# Revit family: Festpunkt Typ AK, T-Stahl, Ø 15 bis  60
name_source: partatom
category: HLS-Bauteile
revit_build: Autodesk Revit 2017 (Build: 20190507_1515(x64)
units: mm (PartAtom-declared; Revit-internal decimal feet)

## family parameters
Arbeitsebenenbasiert = Ja
Beim Laden mit Abzugskörper schneiden = Nein
Bemaßung runder Anschluss = Durchmesser verwenden
Gemeinsam genutzt = Ja
Immer vertikal = Nein
Raumberechnungspunkt = Nein
Teiletyp = Normal

## types (13) — shared parameters
Anzahl Rohrschellen = 6
Aufbaumaß = 50 mm
Ausführung = mit Klemmschelle
Breite Material Rohrschelle = 25 mm
Druckstück Typ I = Druckstück Typ I Gummi
Fabrikat = MEFA
Firma = MEFA Befestigungs- und Montagesysteme GmbH
Kurztext1 = Festpunkt Typ A/K
Länge Profilstahl = 100 mm  [stored 0.328084 ft]
Länge Schweißnase = 81 mm
Mengeneinheit = St
Profilstahltyp = T30
Rohrschellentyp = Maxima PSM
Schalldämmeinlage = Gummi
Stärke Material Rohrschelle = 3 mm
Vorgabe-Ansicht = 1219 mm
max. Temperaturbeständigkeit = 100 °C
vpe = 1 St

## per-type parameters (varying)
| type | Artikelnummer | Breite | EAN | Gewicht | Gewicht pro Bauteil | Höhe 1 | Höhe 2 | Kurztext2 | RA | Rohraußendurchmesser | Rohrschellen Maxima | Rohrschellen ohne |
| Festpunkt Typ AK, T-Stahl, Ø 15, Gummi | 0020153 | 80 mm  [stored 0.262467 ft] | 4250928400048 | 1.43 kg | 1.43 kg | 61 mm |  | 15 mm Gummi mit Klemmschelle | 46 mm  [stored 0.150919 ft] | 15 mm  [stored 0.0492126 ft] | MEFA RS Maxima PSM, Ø15-Ø60 mm, TPE : MEFA RS Maxima PSM,  Ø15 mm, TPE | MEFA RS Maxima PSM, Ø15-Ø60 mm, o.D : MEFA RS Maxima PSM, Ø15 mm, o.D. |
| Festpunkt Typ AK, T-Stahl, Ø 17.2, Gummi | 0020173 | 80 mm  [stored 0.262467 ft] | 4250928400079 | 1.48 kg | 1.48 kg | 63,2 mm |  | 17.2 mm Gummi mit Klemmschelle | 47 mm  [stored 0.154199 ft] | 17 mm | MEFA RS Maxima PSM, Ø15-Ø60 mm, TPE : MEFA RS Maxima PSM,  Ø17,2 mm, TPE | MEFA RS Maxima PSM, Ø15-Ø60 mm, o.D : MEFA RS Maxima PSM, Ø17,2 mm, o.D. |
| Festpunkt Typ AK, T-Stahl, Ø 20, Gummi | 0020203 | 87 mm  [stored 0.285433 ft] | 4250928400086 | 1.52 kg | 1.52 kg | 66 mm |  | 20 mm Gummi mit Klemmschelle | 49 mm  [stored 0.160761 ft] | 20 mm  [stored 0.0656168 ft] | MEFA RS Maxima PSM, Ø15-Ø60 mm, TPE : MEFA RS Maxima PSM, Ø20 mm, TPE | MEFA RS Maxima PSM, Ø15-Ø60 mm, o.D : MEFA RS Maxima PSM, Ø20 mm, o.D. |
| Festpunkt Typ AK, T-Stahl, Ø 21.3, Gummi | 0020223 | 87 mm  [stored 0.285433 ft] | 4250928400123 | 1.52 kg | 1.52 kg | 67,3 mm |  | 21.3 mm Gummi mit Klemmschelle | 49 mm  [stored 0.160761 ft] | 21 mm  [stored 0.0688976 ft] | MEFA RS Maxima PSM, Ø15-Ø60 mm, TPE : MEFA RS Maxima PSM, Ø21,3 mm, TPE | MEFA RS Maxima PSM, Ø15-Ø60 mm, o.D : MEFA RS Maxima PSM, Ø21,3 mm, o.D. |
| Festpunkt Typ AK, T-Stahl, Ø 22- 23, Gummi | 0020233 | 87 mm  [stored 0.285433 ft] | 4250928400130 | 1.52 kg | 1.52 kg | 68 mm | 69 mm | 22 - 23 mm Gummi mit Klemmschelle | 49 mm  [stored 0.160761 ft] | 0 mm  [stored 0 ft] | MEFA RS Maxima PSM, Ø15-Ø60 mm, TPE : MEFA RS Maxima PSM, Ø22-Ø23 mm, TPE | MEFA RS Maxima PSM, Ø15-Ø60 mm, o.D : MEFA RS Maxima PSM, Ø22-Ø23 mm, o.D. |
| Festpunkt Typ AK, T-Stahl, Ø 26- 28, Gummi | 0020273 | 92 mm  [stored 0.301837 ft] | 4250928400178 | 1.58 kg | 1.58 kg | 72 mm | 74 mm | 26 - 28 mm Gummi mit Klemmschelle | 53 mm  [stored 0.173885 ft] | 0 mm  [stored 0 ft] | MEFA RS Maxima PSM, Ø15-Ø60 mm, TPE : MEFA RS Maxima PSM, Ø26-Ø28 mm, TPE | MEFA RS Maxima PSM, Ø15-Ø60 mm, o.D : MEFA RS Maxima PSM, Ø26-Ø28 mm, o.D. |
| Festpunkt Typ AK, T-Stahl, Ø 30, Gummi | 0020303 | 92 mm  [stored 0.301837 ft] | 4250928400185 | 1.62 kg | 1.62 kg | 76 mm |  | 30 mm Gummi mit Klemmschelle | 54 mm | 30 mm  [stored 0.0984252 ft] | MEFA RS Maxima PSM, Ø15-Ø60 mm, TPE : MEFA RS Maxima PSM, Ø30 mm, TPE | MEFA RS Maxima PSM, Ø15-Ø60 mm, o.D : MEFA RS Maxima PSM, Ø30 mm, o.D. |
| Festpunkt Typ AK, T-Stahl, Ø 32- 35, Gummi | 0020343 | 98 mm  [stored 0.321522 ft] | 4250928400222 | 1.65 kg | 1.65 kg | 78 mm | 81 mm | 32 - 35 mm Gummi mit Klemmschelle | 56 mm  [stored 0.183727 ft] | 0 mm  [stored 0 ft] | MEFA RS Maxima PSM, Ø15-Ø60 mm, TPE : MEFA RS Maxima PSM, Ø32-Ø35 mm, TPE | MEFA RS Maxima PSM, Ø15-Ø60 mm, o.D : MEFA RS Maxima PSM, Ø32-Ø35 mm, o.D. |
| Festpunkt Typ AK, T-Stahl, Ø 38- 40, Gummi | 0020403 | 107 mm  [stored 0.35105 ft] | 4250928400246 | 1.72 kg | 1.72 kg | 84 mm | 86 mm | 38 - 40 mm Gummi mit Klemmschelle | 59 mm | 0 mm  [stored 0 ft] | MEFA RS Maxima PSM, Ø15-Ø60 mm, TPE : MEFA RS Maxima PSM, Ø38-Ø40 mm, TPE | MEFA RS Maxima PSM, Ø15-Ø60 mm, o.D : MEFA RS Maxima PSM, Ø38-Ø40 mm, o.D. |
| Festpunkt Typ AK, T-Stahl, Ø 41- 45, Gummi | 0020423 | 107 mm  [stored 0.35105 ft] | 4250928400277 | 1.76 kg | 1.76 kg | 87 mm | 91 mm | 41 - 45 mm Gummi mit Klemmschelle | 61 mm  [stored 0.200131 ft] | 0 mm  [stored 0 ft] | MEFA RS Maxima PSM, Ø15-Ø60 mm, TPE : MEFA RS Maxima PSM, Ø41-Ø45 mm, TPE | MEFA RS Maxima PSM, Ø15-Ø60 mm, o.D : MEFA RS Maxima PSM, Ø41-Ø45 mm, o.D. |
| Festpunkt Typ AK, T-Stahl, Ø 48- 51, Gummi | 0020483 | 114 mm  [stored 0.374016 ft] | 4250928400314 | 1.86 kg | 1.86 kg | 94 mm | 97 mm | 48 - 51 mm Gummi mit Klemmschelle | 64 mm  [stored 0.209974 ft] | 0 mm  [stored 0 ft] | MEFA RS Maxima PSM, Ø15-Ø60 mm, TPE : MEFA RS Maxima PSM, Ø48-Ø51 mm, TPE | MEFA RS Maxima PSM, Ø15-Ø60 mm, o.D : MEFA RS Maxima PSM, Ø48-Ø51 mm, o.D. |
| Festpunkt Typ AK, T-Stahl, Ø 53- 55, Gummi | 0020543 | 120 mm  [stored 0.393701 ft] | 4250928400338 | 1.89 kg | 1.89 kg | 99 mm | 101 mm | 53 - 55 mm Gummi mit Klemmschelle | 66 mm  [stored 0.216535 ft] | 0 mm  [stored 0 ft] | MEFA RS Maxima PSM, Ø15-Ø60 mm, TPE : MEFA RS Maxima PSM, Ø53-Ø55 mm, TPE | MEFA RS Maxima PSM, Ø15-Ø60 mm, o.D : MEFA RS Maxima PSM, Ø53-Ø55 mm, o.D. |
| Festpunkt Typ AK, T-Stahl, Ø 58- 60, Gummi | 0020583 | 129 mm  [stored 0.423228 ft] | 4250928400369 | 1.97 kg | 1.97 kg | 106 mm | 108 mm | 58 - 60 mm Gummi mit Klemmschelle | 69 mm  [stored 0.226378 ft] | 0 mm  [stored 0 ft] | MEFA RS Maxima PSM, Ø15-Ø60 mm, TPE : MEFA RS Maxima PSM, Ø58-Ø60 mm, TPE | MEFA RS Maxima PSM, Ø15-Ø60 mm, o.D : MEFA RS Maxima PSM, Ø58-Ø60 mm, o.D. |

note: [stored X ft] marks values corroborated as IEEE doubles in the binary element streams (Revit-internal decimal feet)

## geometry (parser evidence)
native form markers: Sweep x6
no freeform markers — native parametric forms only
